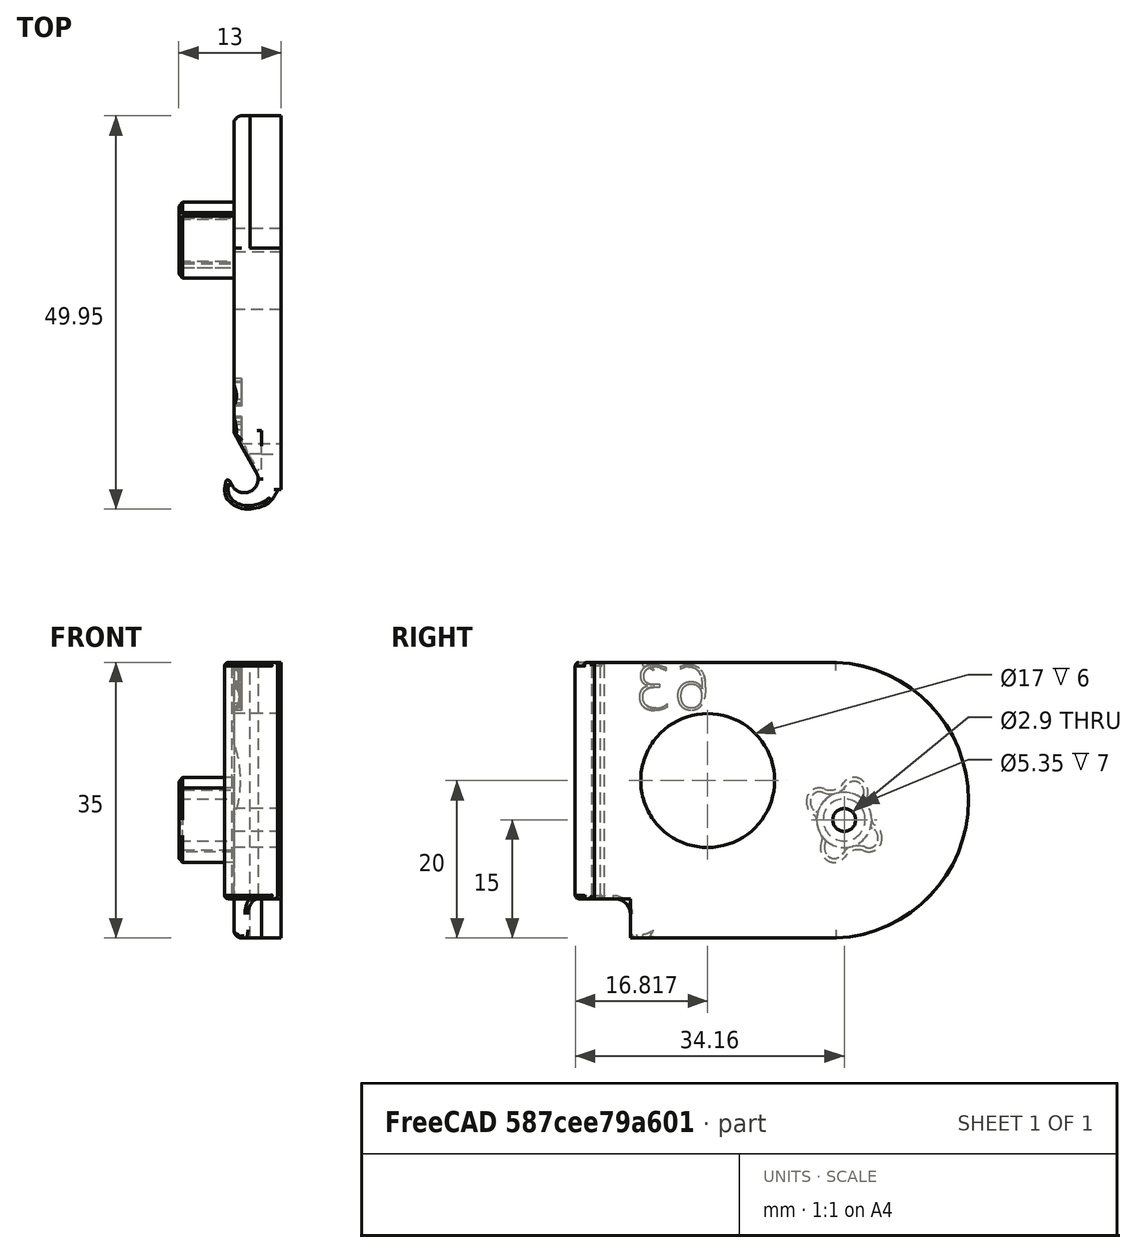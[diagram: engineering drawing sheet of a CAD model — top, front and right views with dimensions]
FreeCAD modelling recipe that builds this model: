
FCSTD DOCUMENT  (FreeCAD 0.18R)
Label: hinge-left-163deg-flat
License: All rights reserved
LicenseURL: http://en.wikipedia.org/wiki/All_rights_reserved
objects: App::FeaturePython×4, Part::FeaturePython×2, Part::Part2DObjectPython×1, Part::Extrusion×1, Part::Cut×1
note: 5 computed .brp shape members not serialized (recipe doc carries the construction recipe); baked Part::Feature solids carry a one-line shape summary decoded from their .brp

FEATURE [Part::FeaturePython] pillar_base_001  label="pillar-base_001"  # a2plus imported part (geometry in sourceFile) (typed FeaturePython)
  Placement = pos=(0.000608724,-1.82326,3.95883) rot=(-1,0,0;0.139801rad)
  a2p_Version = V0.1
  fixedPosition = false
  objectType = a2pPart
  sourceFile = ./parts/pillar-base.fcstd
  subassemblyImport = false
  timeLastImport = 1.60452e+09
  updateColors = true
FEATURE [Part::Part2DObjectPython] ShapeString  # Draft 2D object (typed FeaturePython)
  FontFile = <path>
  Placement = pos=(1.61,10.5,29) rot=(0.57735,-0.57735,-0.57735;2.0944rad)
  Size = 6
  String = 63
  Tracking = 0
FEATURE [Part::Extrusion] Extrude
  Base = -> ShapeString
  Dir = (-1,0,0)
  DirMode = 2
  FaceMakerClass = Part::FaceMakerBullseye
  LengthFwd = 2
  LengthRev = 0
  Solid = false
  Symmetric = false
FEATURE [Part::FeaturePython] bracket_left_flat_001  label="bracket-left-flat_001"  # a2plus imported part (geometry in sourceFile) (typed FeaturePython)
  a2p_Version = V0.1
  fixedPosition = true
  objectType = a2pPart
  sourceFile = ./parts/bracket-left-flat.fcstd
  subassemblyImport = false
  timeLastImport = 1.60454e+09
  updateColors = true
FEATURE [App::FeaturePython] axisCoincident_001  label="axisCoincident_001__bracket-left-flat_001"  # a2plus constraint (typed FeaturePython)
  Object1 = pillar_base_001
  Object2 = bracket_left_flat_001
  ParentTreeObject = -> pillar_base_001
  SubElement1 = Face17
  SubElement2 = Face48
  Suppressed = false
  Type = axial
  directionConstraint = 1
  lockRotation = false
FEATURE [App::FeaturePython] axisCoincident_001_mirror  label="axisCoincident_001__pillar-base_001"  # a2plus constraint (typed FeaturePython)
  Object1 = pillar_base_001
  Object2 = bracket_left_flat_001
  ParentTreeObject = -> bracket_left_flat_001
  SubElement1 = Face17
  SubElement2 = Face48
  Suppressed = false
  Type = axial
  directionConstraint = 1
  lockRotation = false
FEATURE [App::FeaturePython] planeCoincident_001  label="planeCoincident_001__bracket-left-flat_001"  # a2plus constraint (typed FeaturePython)
  Object1 = pillar_base_001
  Object2 = bracket_left_flat_001
  ParentTreeObject = -> pillar_base_001
  SubElement1 = Face1
  SubElement2 = Face72
  Suppressed = false
  Type = plane
  directionConstraint = 0
  offset = 0
FEATURE [App::FeaturePython] planeCoincident_001_mirror  label="planeCoincident_001__pillar-base_001"  # a2plus constraint (typed FeaturePython)
  Object1 = pillar_base_001
  Object2 = bracket_left_flat_001
  ParentTreeObject = -> bracket_left_flat_001
  SubElement1 = Face1
  SubElement2 = Face72
  Suppressed = false
  Type = plane
  directionConstraint = 0
  offset = 0
FEATURE [Part::Cut] Cut
  Base = -> bracket_left_flat_001
  Tool = -> Extrude
note: 1 file-system path scrubbed to <path> (originals preserved in the JSON sidecar)
